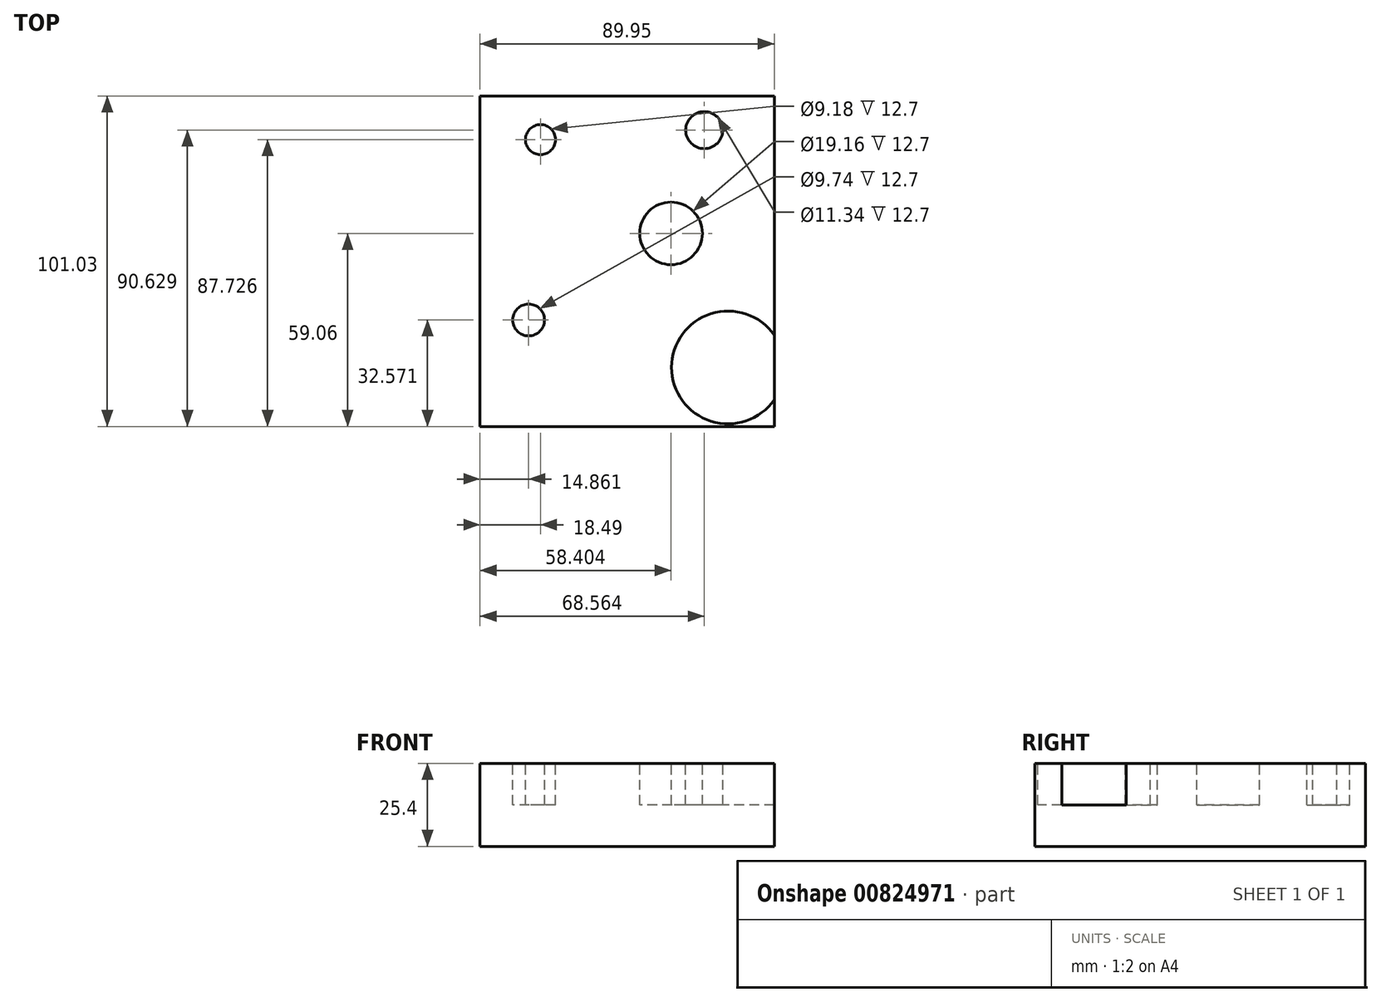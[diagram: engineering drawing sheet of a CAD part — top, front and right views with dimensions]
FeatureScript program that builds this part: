
annotation { "Feature Type Name" : "Feature", "Feature Type Description" : "" }
export const myFeature = defineFeature(function(context is Context, id is Id, definition is map)
    precondition{}
    {
        {
            var Q0;
            Q0=qCreatedBy(makeId("Top.planeOp"),FACE);
            var sketch = newSketch(context, id + "F0", { "sketchPlane" : qUnion([Q0])});
            skLineSegment(sketch, "E0.bottom", {"start": v(-22.44, 41.97) * mm, "end": v(48.6, 41.97) * mm});
            skLineSegment(sketch, "E0.top", {"start": v(-41.35, -59.06) * mm, "end": v(48.6, -59.06) * mm});
            skLineSegment(sketch, "E0.left", {"start": v(-41.35, 41.97) * mm, "end": v(-41.35, -59.06) * mm});
            skLineSegment(sketch, "E0.right", {"start": v(48.6, 41.97) * mm, "end": v(48.6, -59.06) * mm});
            skArc(sketch, "E1", {"start": v(-22.44, 41.97) * mm, "mid": v(-18.53, 25.4) * mm, "end": v(-14.62, 41.97) * mm});
            skCircle(sketch, "E2", {"center": v(23.84, 15.9) * mm, "radius": 11.4 * mm});
            skCircle(sketch, "E3", {"center": v(26.44, -45.38) * mm, "radius": 5.53 * mm});
            skCircle(sketch, "E4", {"center": v(-29.61, -41.47) * mm, "radius": 5.26 * mm});
            skCircle(sketch, "E5", {"center": v(26.44, -15.4) * mm, "radius": 4.75 * mm});
            skCircle(sketch, "E6", {"center": v(-21.14, -21.26) * mm, "radius": 5.87 * mm});
            skCircle(sketch, "E7", {"center": v(38.18, 0) * mm, "radius": 4.96 * mm});
            skArc(sketch, "E8", {"start": v(-41.35, 3.07) * mm, "mid": v(-21.02, 15.24) * mm, "end": v(-41.35, 27.42) * mm});
            skArc(sketch, "E9", {"start": v(-9.53, -59.06) * mm, "mid": v(-16.58, -52.01) * mm, "end": v(-23.63, -59.06) * mm});
            skArc(sketch, "E10", {"start": v(21.04, -59.06) * mm, "mid": v(13.4, -51.44) * mm, "end": v(5.78, -59.06) * mm});
            skArc(sketch, "E11", {"start": v(48.6, -15.57) * mm, "mid": v(31.49, -25.17) * mm, "end": v(48.6, -34.77) * mm});
            skLineSegment(sketch, "E12", {"start": v(-41.35, 41.97) * mm, "end": v(-22.44, 41.97) * mm});
            skSolve(sketch);
        }
        {
            var Q0;
            {var subQ10=sQuery(id+"F0.wireOp",EDGE,"E1");Q0=makeQuery(id+"F0.imprint","IMPRINT",FACE,{"disambiguationData":[TD([[makeQuery(id+"F0.imprint","IMPRINT",EDGE,{"derivedFrom":subQ10}),-1.0]])]});}
            var Q1;
            {var subQ0=sQuery(id+"F0.wireOp",EDGE,"E8");Q1=makeQuery(id+"F0.imprint","IMPRINT",FACE,{"disambiguationData":[TD([[makeQuery(id+"F0.imprint","IMPRINT",EDGE,{"derivedFrom":subQ0}),1.0]])]});}
            var Q2;
            {var subQ0=sQuery(id+"F0.wireOp",EDGE,"E1");Q2=makeQuery(id+"F0.imprint","IMPRINT",FACE,{"disambiguationData":[TD([[makeQuery(id+"F0.imprint","IMPRINT",EDGE,{"derivedFrom":subQ0}),1.0]])]});}
            var Q3;
            Q3=makeQuery(id+"F0.imprint","IMPRINT",FACE,{"disambiguationData":[TD([[makeQuery(id+"F0.imprint","IMPRINT",EDGE,{"derivedFrom":sQuery(id+"F0.wireOp",EDGE,"E2")}),1.0]])]});
            var Q4;
            Q4=makeQuery(id+"F0.imprint","IMPRINT",FACE,{"disambiguationData":[TD([[makeQuery(id+"F0.imprint","IMPRINT",EDGE,{"derivedFrom":sQuery(id+"F0.wireOp",EDGE,"E7")}),1.0]])]});
            var Q5;
            Q5=makeQuery(id+"F0.imprint","IMPRINT",FACE,{"disambiguationData":[TD([[makeQuery(id+"F0.imprint","IMPRINT",EDGE,{"derivedFrom":sQuery(id+"F0.wireOp",EDGE,"E5")}),1.0]])]});
            var Q6;
            Q6=makeQuery(id+"F0.imprint","IMPRINT",FACE,{"disambiguationData":[TD([[makeQuery(id+"F0.imprint","IMPRINT",EDGE,{"derivedFrom":sQuery(id+"F0.wireOp",EDGE,"E6")}),1.0]])]});
            var Q7;
            {var subQ0=sQuery(id+"F0.wireOp",EDGE,"E11");Q7=makeQuery(id+"F0.imprint","IMPRINT",FACE,{"disambiguationData":[TD([[makeQuery(id+"F0.imprint","IMPRINT",EDGE,{"derivedFrom":subQ0}),1.0]])]});}
            var Q8;
            Q8=makeQuery(id+"F0.imprint","IMPRINT",FACE,{"disambiguationData":[TD([[makeQuery(id+"F0.imprint","IMPRINT",EDGE,{"derivedFrom":sQuery(id+"F0.wireOp",EDGE,"E3")}),1.0]])]});
            var Q9;
            {var subQ0=sQuery(id+"F0.wireOp",EDGE,"E10");Q9=makeQuery(id+"F0.imprint","IMPRINT",FACE,{"disambiguationData":[TD([[makeQuery(id+"F0.imprint","IMPRINT",EDGE,{"derivedFrom":subQ0}),1.0]])]});}
            var Q10;
            {var subQ0=sQuery(id+"F0.wireOp",EDGE,"E9");Q10=makeQuery(id+"F0.imprint","IMPRINT",FACE,{"disambiguationData":[TD([[makeQuery(id+"F0.imprint","IMPRINT",EDGE,{"derivedFrom":subQ0}),1.0]])]});}
            var Q11;
            Q11=makeQuery(id+"F0.imprint","IMPRINT",FACE,{"disambiguationData":[TD([[makeQuery(id+"F0.imprint","IMPRINT",EDGE,{"derivedFrom":sQuery(id+"F0.wireOp",EDGE,"E4")}),1.0]])]});
            extrude(context, id + "F1", {"entities" : qUnion([Q0, Q1, Q2, Q3, Q4, Q5, Q6, Q7, Q8, Q9, Q10, Q11]), "depth" : 25.4 * mm, "offsetDistance" : 25.4 * mm});
        }
        {
            var Q0;
            Q0=makeQuery(id+"F1.opExtrude","CAP_FACE",FACE,{"disambiguationData":[OSD([sQuery(id+"F0.wireOp",EDGE,"E0.bottom"),sQuery(id+"F0.wireOp",EDGE,"E0.top"),sQuery(id+"F0.wireOp",EDGE,"E0.left"),sQuery(id+"F0.wireOp",EDGE,"E0.right"),sQuery(id+"F0.wireOp",EDGE,"E12")])],"isStart":false});
            var sketch = newSketch(context, id + "F2", { "sketchPlane" : qUnion([Q0])});
            skCircle(sketch, "E13", {"center": v(-22.86, 28.67) * mm, "radius": 4.59 * mm});
            skCircle(sketch, "E14", {"center": v(27.21, 31.57) * mm, "radius": 5.67 * mm});
            skCircle(sketch, "E15", {"center": v(-26.49, -26.49) * mm, "radius": 4.87 * mm});
            skCircle(sketch, "E16", {"center": v(17.05, 0) * mm, "radius": 9.58 * mm});
            skArc(sketch, "E17", {"start": v(48.6, -31.11) * mm, "mid": v(17.22, -41) * mm, "end": v(48.6, -50.9) * mm});
            skLineSegment(sketch, "E18", {"start": v(48.6, -31.11) * mm, "end": v(48.6, -50.9) * mm});
            skSolve(sketch);
        }
        {
            var Q0;
            Q0 = qSketchRegion(id + "F2", true);
            extrude(context, id + "F3", {"entities" : qUnion([Q0]), "operationType" : NewBodyOperationType.REMOVE, "oppositeDirection" : true, "depth" : 12.7 * mm, "offsetDistance" : 25.4 * mm});
        }
    });
